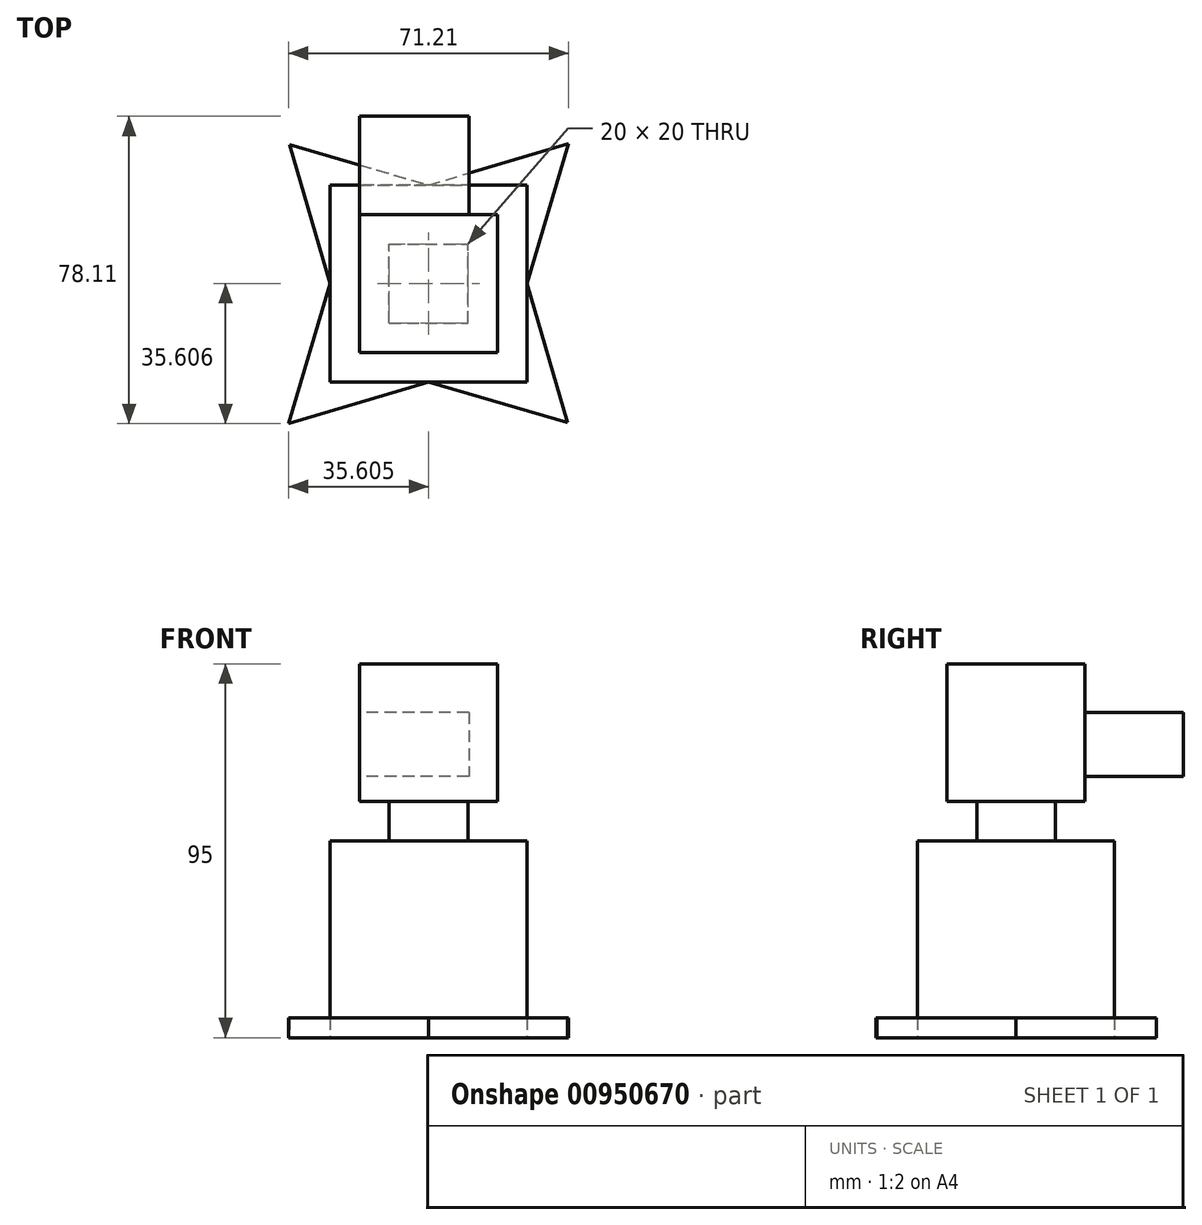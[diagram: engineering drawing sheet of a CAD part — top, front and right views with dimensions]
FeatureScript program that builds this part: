
annotation { "Feature Type Name" : "Feature", "Feature Type Description" : "" }
export const myFeature = defineFeature(function(context is Context, id is Id, definition is map)
    precondition{}
    {
        {
            var Q0;
            Q0=qCreatedBy(makeId("Top.planeOp"),FACE);
            var sketch = newSketch(context, id + "F0", { "sketchPlane" : qUnion([Q0])});
            skLineSegment(sketch, "E0.bottom", {"start": v(-35.22, 20.7) * mm, "end": v(14.78, 20.7) * mm});
            skLineSegment(sketch, "E0.top", {"start": v(-35.22, -29.3) * mm, "end": v(14.78, -29.3) * mm});
            skLineSegment(sketch, "E0.left", {"start": v(-35.22, 20.7) * mm, "end": v(-35.22, -29.3) * mm});
            skLineSegment(sketch, "E0.right", {"start": v(14.78, 20.7) * mm, "end": v(14.78, -29.3) * mm});
            skLineSegment(sketch, "E1.top", {"start": v(-10.22, 20.7) * mm, "end": v(0, 20.7) * mm});
            skSolve(sketch);
        }
        {
            var Q0;
            Q0=makeQuery(id+"F0.imprint","IMPRINT",FACE,{"disambiguationData":[TD([[makeQuery(id+"F0.imprint","IMPRINT",EDGE,{"derivedFrom":sQuery(id+"F0.wireOp",EDGE,"E0.top")}),1.0]])]});
            extrude(context, id + "F1", {"entities" : qUnion([Q0]), "depth" : 50 * mm, "offsetDistance" : 25 * mm});
        }
        {
            var Q0;
            Q0=makeQuery(id+"F1.opExtrude","CAP_FACE",FACE,{"disambiguationData":[OSD([sQuery(id+"F0.wireOp",EDGE,"E0.bottom"),sQuery(id+"F0.wireOp",EDGE,"E0.top"),sQuery(id+"F0.wireOp",EDGE,"E0.left"),sQuery(id+"F0.wireOp",EDGE,"E0.right"),sQuery(id+"F0.wireOp",EDGE,"E1.top")])],"isStart":false});
            var sketch = newSketch(context, id + "F2", { "sketchPlane" : qUnion([Q0])});
            skLineSegment(sketch, "E2.bottom", {"start": v(-20.22, -14.3) * mm, "end": v(-0.22, -14.3) * mm});
            skLineSegment(sketch, "E2.top", {"start": v(-20.22, 5.7) * mm, "end": v(-0.22, 5.7) * mm});
            skLineSegment(sketch, "E2.left", {"start": v(-20.22, -14.3) * mm, "end": v(-20.22, 5.7) * mm});
            skLineSegment(sketch, "E2.right", {"start": v(-0.22, -14.3) * mm, "end": v(-0.22, 5.7) * mm});
            skPoint(sketch, "E2.middle", {"position": v(-10.22, -4.3) * mm});
            skPoint(sketch, "E2.middle.positionSnap0", {"position": v(-10.22, -29.3) * mm});
            skPoint(sketch, "E2.middle.positionSnap1", {"position": v(-35.22, -4.3) * mm});
            skPoint(sketch, "E2.centerSnap0", {"position": v(-10.22, -29.3) * mm});
            skPoint(sketch, "E2.centerSnap1", {"position": v(-35.22, -4.3) * mm});
            skSolve(sketch);
        }
        {
            var Q0;
            Q0 = qSketchRegion(id + "F2", true);
            extrude(context, id + "F3", {"entities" : qUnion([Q0]), "operationType" : NewBodyOperationType.ADD, "depth" : 10 * mm, "offsetDistance" : 25 * mm});
        }
        {
            var Q0;
            Q0=makeQuery(id+"F3.opExtrude","CAP_FACE",FACE,{"disambiguationData":[OSD([sQuery(id+"F2.wireOp",EDGE,"E2.bottom"),sQuery(id+"F2.wireOp",EDGE,"E2.top"),sQuery(id+"F2.wireOp",EDGE,"E2.left"),sQuery(id+"F2.wireOp",EDGE,"E2.right")])],"isStart":false});
            var sketch = newSketch(context, id + "F4", { "sketchPlane" : qUnion([Q0])});
            skLineSegment(sketch, "E3.bottom", {"start": v(7.28, -21.8) * mm, "end": v(-27.72, -21.8) * mm});
            skLineSegment(sketch, "E3.top", {"start": v(7.28, 13.2) * mm, "end": v(-27.72, 13.2) * mm});
            skLineSegment(sketch, "E3.left", {"start": v(7.28, -21.8) * mm, "end": v(7.28, 13.2) * mm});
            skLineSegment(sketch, "E3.right", {"start": v(-27.72, -21.8) * mm, "end": v(-27.72, 13.2) * mm});
            skPoint(sketch, "E3.middle", {"position": v(-10.22, -4.3) * mm});
            skPoint(sketch, "E3.middle.positionSnap0", {"position": v(-20.22, -4.3) * mm});
            skPoint(sketch, "E3.middle.positionSnap1", {"position": v(-10.22, 5.7) * mm});
            skPoint(sketch, "E3.centerSnap0", {"position": v(-20.22, -4.3) * mm});
            skPoint(sketch, "E3.centerSnap1", {"position": v(-10.22, 5.7) * mm});
            skSolve(sketch);
        }
        {
            var Q0;
            Q0 = qSketchRegion(id + "F4", true);
            extrude(context, id + "F5", {"entities" : qUnion([Q0]), "operationType" : NewBodyOperationType.ADD, "depth" : 35 * mm, "offsetDistance" : 25 * mm});
        }
        {
            var Q0;
            Q0=makeQuery(id+"F1.opExtrude","CAP_FACE",FACE,{"disambiguationData":[OSD([sQuery(id+"F0.wireOp",EDGE,"E0.bottom"),sQuery(id+"F0.wireOp",EDGE,"E0.top"),sQuery(id+"F0.wireOp",EDGE,"E0.left"),sQuery(id+"F0.wireOp",EDGE,"E0.right"),sQuery(id+"F0.wireOp",EDGE,"E1.top")])],"isStart":true});
            var sketch = newSketch(context, id + "F6", { "sketchPlane" : qUnion([Q0])});
            skLineSegment(sketch, "E4", {"start": v(-45.82, 39.9) * mm, "end": v(-10.22, 29.3) * mm});
            skLineSegment(sketch, "E5", {"start": v(-45.82, 39.9) * mm, "end": v(-35.22, 4.3) * mm});
            skLineSegment(sketch, "E6", {"start": v(25.14, 39.65) * mm, "end": v(-10.22, 29.3) * mm});
            skLineSegment(sketch, "E7", {"start": v(25.14, 39.65) * mm, "end": v(14.78, 4.3) * mm});
            skLineSegment(sketch, "E8", {"start": v(14.78, 4.3) * mm, "end": v(25.4, -31.31) * mm});
            skLineSegment(sketch, "E9", {"start": v(-35.22, 4.3) * mm, "end": v(-45.57, -31.06) * mm});
            skLineSegment(sketch, "E10", {"start": v(-45.57, -31.06) * mm, "end": v(-10.22, -20.7) * mm});
            skLineSegment(sketch, "E11", {"start": v(-10.22, -20.7) * mm, "end": v(25.4, -31.31) * mm});
            skSolve(sketch);
        }
        {
            var Q0;
            Q0 = qSketchRegion(id + "F6", true);
            extrude(context, id + "F7", {"entities" : qUnion([Q0]), "operationType" : NewBodyOperationType.ADD, "oppositeDirection" : true, "depth" : 5 * mm, "offsetDistance" : 25 * mm});
        }
        {
            var Q0;
            Q0=makeQuery(id+"F5.opExtrude","SWEPT_FACE",FACE,{"disambiguationData":[OSD([sQuery(id+"F4.wireOp",EDGE,"E3.top")])]});
            var sketch = newSketch(context, id + "F8", { "sketchPlane" : qUnion([Q0])});
            skLineSegment(sketch, "E12.bottom", {"start": v(0, 82.67) * mm, "end": v(27.72, 82.67) * mm});
            skLineSegment(sketch, "E12.top", {"start": v(0, 66.41) * mm, "end": v(27.72, 66.41) * mm});
            skLineSegment(sketch, "E12.left", {"start": v(0, 82.67) * mm, "end": v(0, 66.41) * mm});
            skLineSegment(sketch, "E12.right", {"start": v(27.72, 82.67) * mm, "end": v(27.72, 66.41) * mm});
            skSolve(sketch);
        }
        {
            var Q0;
            Q0=makeQuery(id+"F8.imprint","IMPRINT",FACE,{"disambiguationData":[TD([[makeQuery(id+"F8.imprint","IMPRINT",EDGE,{"derivedFrom":sQuery(id+"F8.wireOp",EDGE,"E12.bottom")}),-1.0]])]});
            extrude(context, id + "F9", {"entities" : qUnion([Q0]), "operationType" : NewBodyOperationType.ADD, "depth" : 25 * mm, "offsetDistance" : 25 * mm});
        }
    });
